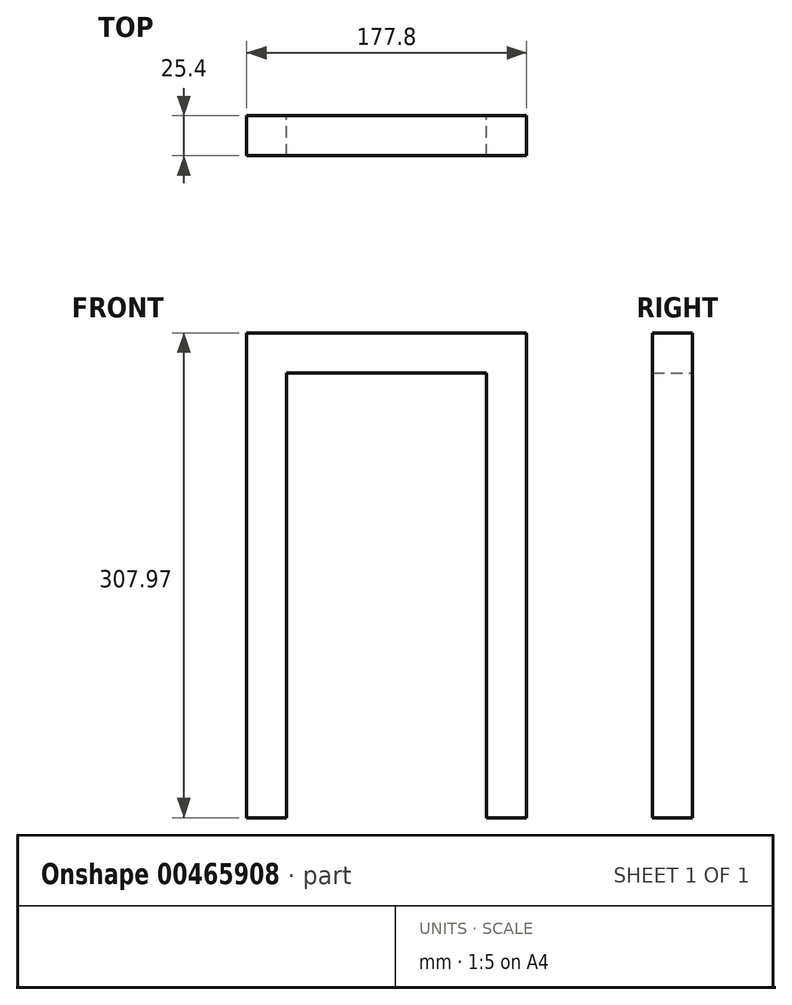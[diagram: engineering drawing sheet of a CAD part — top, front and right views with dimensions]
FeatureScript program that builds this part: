
annotation { "Feature Type Name" : "Feature", "Feature Type Description" : "" }
export const myFeature = defineFeature(function(context is Context, id is Id, definition is map)
    precondition{}
    {
        {
            var Q0;
            Q0=qCreatedBy(makeId("Front.planeOp"),FACE);
            var sketch = newSketch(context, id + "F0", { "sketchPlane" : qUnion([Q0])});
            skLineSegment(sketch, "E0.bottom", {"start": v(-7.92, -8.34) * mm, "end": v(-33.32, -8.34) * mm});
            skLineSegment(sketch, "E0.top", {"start": v(-7.92, 299.63) * mm, "end": v(-33.32, 299.63) * mm});
            skLineSegment(sketch, "E0.left", {"start": v(-7.92, -8.34) * mm, "end": v(-7.92, 299.63) * mm});
            skLineSegment(sketch, "E0.right", {"start": v(-33.32, -8.34) * mm, "end": v(-33.32, 299.63) * mm});
            skLineSegment(sketch, "E1.bottom", {"start": v(-7.92, 299.63) * mm, "end": v(119.08, 299.63) * mm});
            skLineSegment(sketch, "E1.top", {"start": v(-7.92, 274.23) * mm, "end": v(119.08, 274.23) * mm});
            skLineSegment(sketch, "E1.left", {"start": v(-7.92, 299.63) * mm, "end": v(-7.92, 274.23) * mm});
            skLineSegment(sketch, "E1.right", {"start": v(119.08, 299.63) * mm, "end": v(119.08, 274.23) * mm});
            skLineSegment(sketch, "E2.bottom", {"start": v(119.08, 299.63) * mm, "end": v(144.48, 299.63) * mm});
            skLineSegment(sketch, "E2.top", {"start": v(119.08, -8.34) * mm, "end": v(144.48, -8.34) * mm});
            skLineSegment(sketch, "E2.left", {"start": v(119.08, 299.63) * mm, "end": v(119.08, -8.34) * mm});
            skLineSegment(sketch, "E2.right", {"start": v(144.48, 299.63) * mm, "end": v(144.48, -8.34) * mm});
            skSolve(sketch);
        }
        {
            var Q0;
            {var subQ3=sQuery(id+"F0.wireOp",EDGE,"E2.bottom");Q0=makeQuery(id+"F0.imprint","IMPRINT",FACE,{"disambiguationData":[TD([[makeQuery(id+"F0.imprint","IMPRINT",EDGE,{"derivedFrom":subQ3}),-1.0]])]});}
            var Q1;
            {var subQ0=sQuery(id+"F0.wireOp",EDGE,"E1.bottom");Q1=makeQuery(id+"F0.imprint","IMPRINT",FACE,{"disambiguationData":[TD([[makeQuery(id+"F0.imprint","IMPRINT",EDGE,{"derivedFrom":subQ0}),-1.0]])]});}
            var Q2;
            Q2=makeQuery(id+"F0.imprint","IMPRINT",FACE,{"disambiguationData":[TD([[makeQuery(id+"F0.imprint","IMPRINT",EDGE,{"derivedFrom":sQuery(id+"F0.wireOp",EDGE,"E0.bottom")}),-1.0]])]});
            extrude(context, id + "F1", {"entities" : qUnion([Q0, Q1, Q2]), "depth" : 25.4 * mm});
        }
    });
